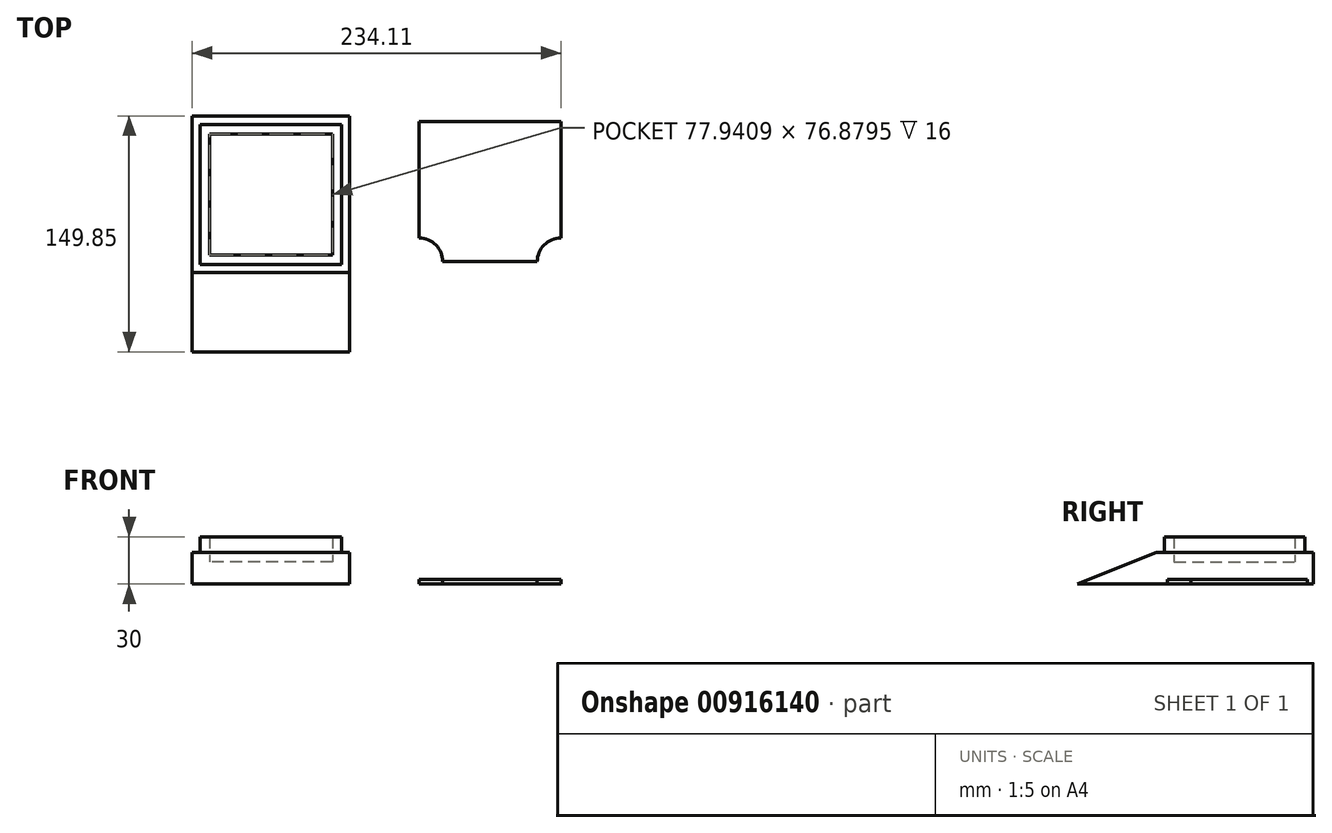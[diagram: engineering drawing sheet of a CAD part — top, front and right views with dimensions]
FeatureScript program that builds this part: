
annotation { "Feature Type Name" : "Feature", "Feature Type Description" : "" }
export const myFeature = defineFeature(function(context is Context, id is Id, definition is map)
    precondition{}
    {
        {
            var Q0;
            Q0=qCreatedBy(makeId("Top.planeOp"),FACE);
            var sketch = newSketch(context, id + "F0", { "sketchPlane" : qUnion([Q0])});
            skLineSegment(sketch, "E0.bottom", {"start": v(-50, 50) * mm, "end": v(50, 50) * mm});
            skLineSegment(sketch, "E0.top", {"start": v(-50, -50) * mm, "end": v(50, -50) * mm});
            skLineSegment(sketch, "E0.left", {"start": v(-50, 50) * mm, "end": v(-50, -50) * mm});
            skLineSegment(sketch, "E0.right", {"start": v(50, 50) * mm, "end": v(50, -50) * mm});
            skPoint(sketch, "E0.middle", {"position": v(0, 0) * mm});
            skLineSegment(sketch, "E1.top", {"start": v(-50, -99.85) * mm, "end": v(50, -99.85) * mm});
            skLineSegment(sketch, "E1.left", {"start": v(-50, -50) * mm, "end": v(-50, -99.85) * mm});
            skLineSegment(sketch, "E1.right", {"start": v(50, -50) * mm, "end": v(50, -99.85) * mm});
            skSolve(sketch);
        }
        {
            var Q0;
            Q0 = qSketchRegion(id + "F0", true);
            extrude(context, id + "F1", {"entities" : qUnion([Q0]), "depth" : 20 * mm, "offsetDistance" : 25 * mm});
        }
        {
            var Q0;
            Q0=makeQuery(id+"F1.opExtrude","SWEPT_FACE",FACE,{"disambiguationData":[OSD([sQuery(id+"F0.wireOp",EDGE,"E0.right"),sQuery(id+"F0.wireOp",EDGE,"E1.right")])]});
            var sketch = newSketch(context, id + "F2", { "sketchPlane" : qUnion([Q0])});
            skLineSegment(sketch, "E2", {"start": v(-99.85, 0) * mm, "end": v(-49.55, 20) * mm});
            skLineSegment(sketch, "E3", {"start": v(-49.55, 20) * mm, "end": v(-99.85, 20) * mm});
            skLineSegment(sketch, "E4", {"start": v(-99.85, 20) * mm, "end": v(-99.85, 0) * mm});
            skSolve(sketch);
        }
        {
            var Q0;
            Q0 = qSketchRegion(id + "F2", true);
            extrude(context, id + "F3", {"entities" : qUnion([Q0]), "operationType" : NewBodyOperationType.REMOVE, "endBound" : BoundingType.THROUGH_ALL, "oppositeDirection" : true, "depth" : 25 * mm, "offsetDistance" : 25 * mm});
        }
        {
            var Q0;
            Q0=makeQuery(id+"F1.opExtrude","CAP_FACE",FACE,{"disambiguationData":[OSD([sQuery(id+"F0.wireOp",EDGE,"E0.bottom"),sQuery(id+"F0.wireOp",EDGE,"E0.left"),sQuery(id+"F0.wireOp",EDGE,"E0.right"),sQuery(id+"F0.wireOp",EDGE,"E1.top"),sQuery(id+"F0.wireOp",EDGE,"E1.left"),sQuery(id+"F0.wireOp",EDGE,"E1.right")])],"isStart":false});
            var sketch = newSketch(context, id + "F4", { "sketchPlane" : qUnion([Q0])});
            skPoint(sketch, "E5", {"position": v(-45, -44.55) * mm});
            skPoint(sketch, "E6", {"position": v(45, -44.55) * mm});
            skPoint(sketch, "E7.startSnap0", {"position": v(-50, 0.23) * mm});
            skPoint(sketch, "E8.MirrorP", {"position": v(-45, 44.55) * mm});
            skPoint(sketch, "E9.MirrorP", {"position": v(45, 44.55) * mm});
            skLineSegment(sketch, "E10.bottom", {"start": v(-45, -44.55) * mm, "end": v(-38.92, -44.55) * mm});
            skLineSegment(sketch, "E10.top", {"start": v(-45, 44.55) * mm, "end": v(-38.92, 44.55) * mm});
            skLineSegment(sketch, "E10.left", {"start": v(-45, -44.55) * mm, "end": v(-45, 44.55) * mm});
            skLineSegment(sketch, "E10.right", {"start": v(-38.92, -44.55) * mm, "end": v(-38.92, 44.55) * mm});
            skLineSegment(sketch, "E11.bottom", {"start": v(-45, 44.55) * mm, "end": v(45, 44.55) * mm});
            skLineSegment(sketch, "E11.top", {"start": v(-45, 38.51) * mm, "end": v(45, 38.51) * mm});
            skLineSegment(sketch, "E11.left", {"start": v(-45, 44.55) * mm, "end": v(-45, 38.51) * mm});
            skLineSegment(sketch, "E11.right", {"start": v(45, 44.55) * mm, "end": v(45, 38.51) * mm});
            skLineSegment(sketch, "E12.bottom", {"start": v(45, -44.55) * mm, "end": v(39.03, -44.55) * mm});
            skLineSegment(sketch, "E12.top", {"start": v(45, 44.55) * mm, "end": v(39.03, 44.55) * mm});
            skLineSegment(sketch, "E12.left", {"start": v(45, -44.55) * mm, "end": v(45, 44.55) * mm});
            skLineSegment(sketch, "E12.right", {"start": v(39.03, -44.55) * mm, "end": v(39.03, 44.55) * mm});
            skLineSegment(sketch, "E13.bottom", {"start": v(45, -44.55) * mm, "end": v(-45, -44.55) * mm});
            skLineSegment(sketch, "E13.top", {"start": v(45, -38.37) * mm, "end": v(-45, -38.37) * mm});
            skLineSegment(sketch, "E13.left", {"start": v(45, -44.55) * mm, "end": v(45, -38.37) * mm});
            skLineSegment(sketch, "E13.right", {"start": v(-45, -44.55) * mm, "end": v(-45, -38.37) * mm});
            skSolve(sketch);
        }
        {
            var Q0;
            Q0 = qSketchRegion(id + "F4", true);
            extrude(context, id + "F5", {"entities" : qUnion([Q0]), "operationType" : NewBodyOperationType.ADD, "depth" : 10 * mm, "offsetDistance" : 25 * mm});
        }
        {
            var Q0;
            Q0=makeQuery(id+"F5.boolean.opBoolean","SPLIT",FACE,{"disambiguationData":[TD([makeQuery(id+"F5.opExtrude","SWEPT_FACE",FACE,{"disambiguationData":[OSD([sQuery(id+"F4.wireOp",EDGE,"E10.right")])]})])],"derivedFrom":makeQuery(id+"F1.opExtrude","CAP_FACE",FACE,{"disambiguationData":[OSD([sQuery(id+"F0.wireOp",EDGE,"E0.bottom"),sQuery(id+"F0.wireOp",EDGE,"E0.left"),sQuery(id+"F0.wireOp",EDGE,"E0.right"),sQuery(id+"F0.wireOp",EDGE,"E1.top"),sQuery(id+"F0.wireOp",EDGE,"E1.left"),sQuery(id+"F0.wireOp",EDGE,"E1.right")])],"isStart":false})});
            extrude(context, id + "F6", {"entities" : qUnion([Q0]), "operationType" : NewBodyOperationType.REMOVE, "oppositeDirection" : true, "depth" : 6 * mm, "offsetDistance" : 25 * mm});
        }
        {
            var Q0;
            Q0=qCreatedBy(makeId("Top.planeOp"),FACE);
            var sketch = newSketch(context, id + "F7", { "sketchPlane" : qUnion([Q0])});
            skLineSegment(sketch, "E14.bottom", {"start": v(94.11, 46.45) * mm, "end": v(184.11, 46.45) * mm});
            skLineSegment(sketch, "E14.top", {"start": v(94.11, -42.55) * mm, "end": v(184.11, -42.55) * mm});
            skLineSegment(sketch, "E14.left", {"start": v(94.11, 46.45) * mm, "end": v(94.11, -42.55) * mm});
            skLineSegment(sketch, "E14.right", {"start": v(184.11, 46.45) * mm, "end": v(184.11, -42.55) * mm});
            skSolve(sketch);
        }
        {
            var Q0;
            Q0 = qSketchRegion(id + "F7", true);
            extrude(context, id + "F8", {"entities" : qUnion([Q0]), "depth" : 3 * mm, "offsetDistance" : 25 * mm});
        }
        {
            var Q0;
            Q0=makeQuery(id+"F8.opExtrude","CAP_FACE",FACE,{"disambiguationData":[OSD([sQuery(id+"F7.wireOp",EDGE,"E14.bottom"),sQuery(id+"F7.wireOp",EDGE,"E14.top"),sQuery(id+"F7.wireOp",EDGE,"E14.left"),sQuery(id+"F7.wireOp",EDGE,"E14.right")])],"isStart":false});
            var sketch = newSketch(context, id + "F9", { "sketchPlane" : qUnion([Q0])});
            skArc(sketch, "E15", {"start": v(109.11, -42.55) * mm, "mid": v(104.72, -31.94) * mm, "end": v(94.11, -27.55) * mm});
            skArc(sketch, "E16", {"start": v(184.11, -27.55) * mm, "mid": v(173.5, -31.94) * mm, "end": v(169.11, -42.55) * mm});
            skSolve(sketch);
        }
        {
            var Q0;
            Q0 = qSketchRegion(id + "F9", true);
            var Q1;
            {var subQ0=sQuery(id+"F9.wireOp",EDGE,"E15");Q1=makeQuery(id+"F9.imprint","IMPRINT",FACE,{"disambiguationData":[TD([[makeQuery(id+"F9.imprint","IMPRINT",EDGE,{"derivedFrom":subQ0}),1.0]])]});}
            var Q2;
            {var subQ0=sQuery(id+"F9.wireOp",EDGE,"E16");Q2=makeQuery(id+"F9.imprint","IMPRINT",FACE,{"disambiguationData":[TD([[makeQuery(id+"F9.imprint","IMPRINT",EDGE,{"derivedFrom":subQ0}),1.0]])]});}
            extrude(context, id + "F10", {"entities" : qUnion([Q0, Q1, Q2]), "operationType" : NewBodyOperationType.REMOVE, "oppositeDirection" : true, "depth" : 25 * mm, "offsetDistance" : 25 * mm});
        }
    });
